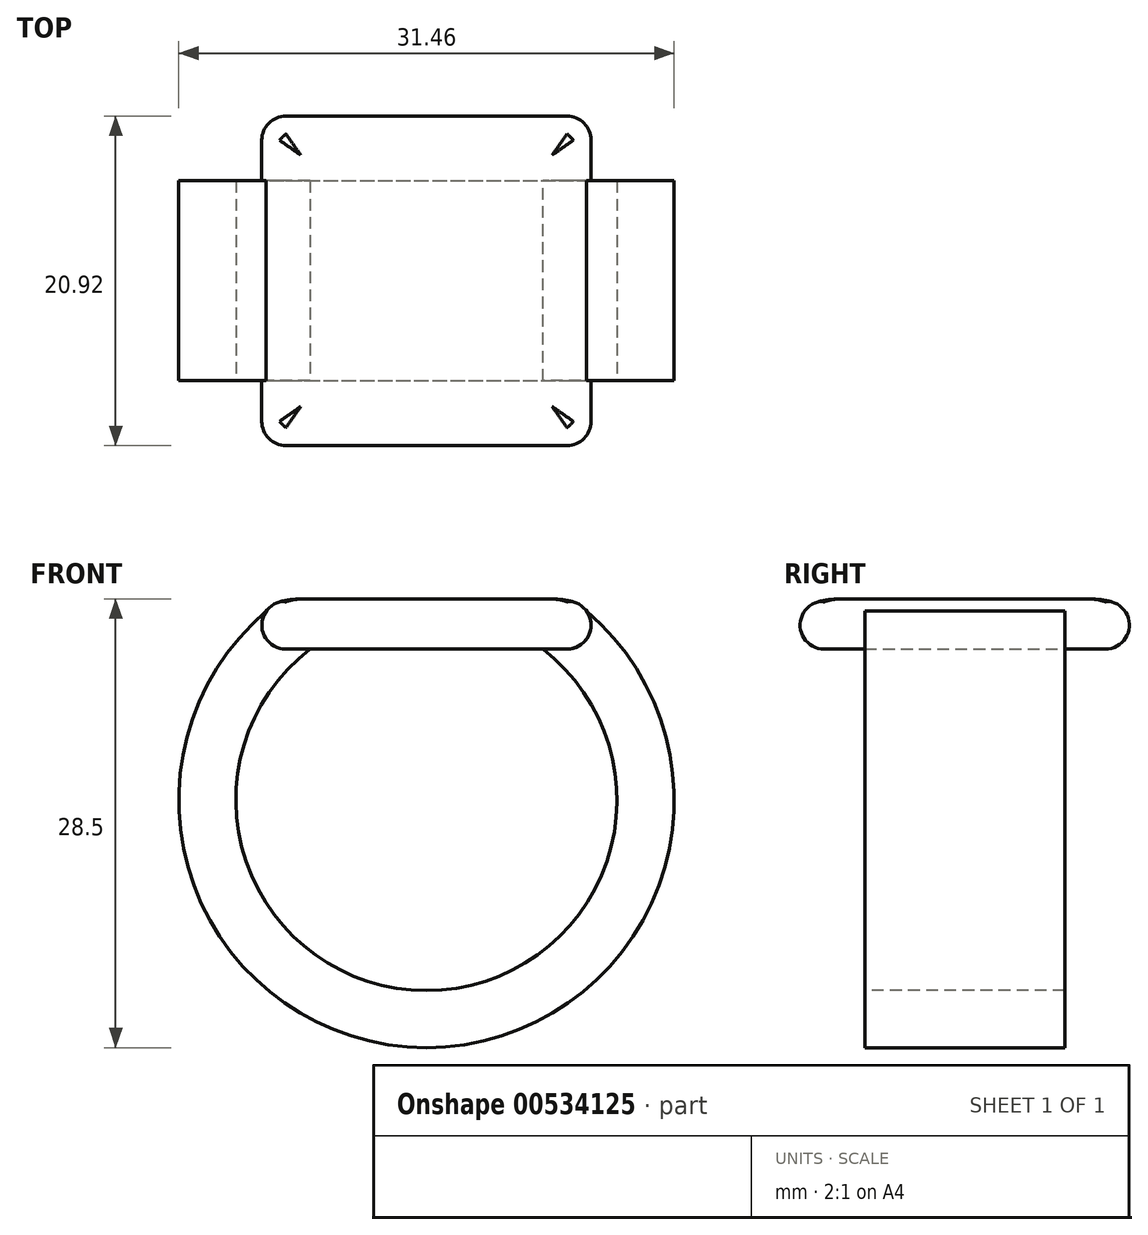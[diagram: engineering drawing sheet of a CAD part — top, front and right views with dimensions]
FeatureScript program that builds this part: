
annotation { "Feature Type Name" : "Feature", "Feature Type Description" : "" }
export const myFeature = defineFeature(function(context is Context, id is Id, definition is map)
    precondition{}
    {
        {
            var Q0;
            Q0=qCreatedBy(makeId("Top.planeOp"),FACE);
            var sketch = newSketch(context, id + "F0", { "sketchPlane" : qUnion([Q0])});
            skLineSegment(sketch, "E0.bottom", {"start": v(12.7, 12.7) * mm, "end": v(-12.7, 12.7) * mm});
            skLineSegment(sketch, "E0.top", {"start": v(12.7, -12.7) * mm, "end": v(-12.7, -12.7) * mm});
            skLineSegment(sketch, "E0.left", {"start": v(12.7, 12.7) * mm, "end": v(12.7, -12.7) * mm});
            skLineSegment(sketch, "E0.right", {"start": v(-12.7, 12.7) * mm, "end": v(-12.7, -12.7) * mm});
            skPoint(sketch, "E0.middle", {"position": v(0, 0) * mm});
            skSolve(sketch);
        }
        {
            var Q0;
            Q0=makeQuery(id+"F0.imprint","IMPRINT",FACE,{"disambiguationData":[TD([[makeQuery(id+"F0.imprint","IMPRINT",EDGE,{"derivedFrom":sQuery(id+"F0.wireOp",EDGE,"E0.bottom")}),1.0]])]});
            extrude(context, id + "F1", {"entities" : qUnion([Q0]), "depth" : 3.17 * mm, "offsetDistance" : 25.4 * mm});
        }
        {
            var Q0;
            Q0=qCreatedBy(makeId("Front.planeOp"),FACE);
            var sketch = newSketch(context, id + "F2", { "sketchPlane" : qUnion([Q0])});
            skArc(sketch, "E1", {"start": v(-10.16, 0) * mm, "mid": v(0, -23.56) * mm, "end": v(10.16, 0) * mm});
            skSolve(sketch);
        }
        {
            var Q0;
            Q0=makeQuery(id+"F1.opExtrude","CAP_FACE",FACE,{"disambiguationData":[OSD([sQuery(id+"F0.wireOp",EDGE,"E0.bottom"),sQuery(id+"F0.wireOp",EDGE,"E0.top"),sQuery(id+"F0.wireOp",EDGE,"E0.left"),sQuery(id+"F0.wireOp",EDGE,"E0.right")])],"isStart":true});
            var sketch = newSketch(context, id + "F3", { "sketchPlane" : qUnion([Q0])});
            skLineSegment(sketch, "E2.bottom", {"start": v(-12.47, -6.35) * mm, "end": v(-7.39, -6.35) * mm});
            skLineSegment(sketch, "E2.top", {"start": v(-12.47, 6.35) * mm, "end": v(-7.39, 6.35) * mm});
            skLineSegment(sketch, "E2.left", {"start": v(-12.47, -6.35) * mm, "end": v(-12.47, 6.35) * mm});
            skLineSegment(sketch, "E2.right", {"start": v(-7.39, -6.35) * mm, "end": v(-7.39, 6.35) * mm});
            skPoint(sketch, "E2.middle", {"position": v(-9.93, 0) * mm});
            skSolve(sketch);
        }
        {
            var Q0;
            Q0 = qSketchRegion(id + "F3", true);
            var Q1;
            Q1 = qConstructionFilter(qBodyType(qCreatedBy(id + "F2" ,EDGE), BodyType.WIRE), ConstructionObject.NO);
            sweep(context, id + "F4", {"operationType" : NewBodyOperationType.ADD, "profiles" : qUnion([Q0]), "path" : qUnion([Q1])});
        }
        {
            var Q0;
            Q0=qCreatedBy(makeId("Front.planeOp"),FACE);
            var sketch = newSketch(context, id + "F5", { "sketchPlane" : qUnion([Q0])});
            skLineSegment(sketch, "E3.0", {"start": v(10.16, 0) * mm, "end": v(7.39, 0) * mm});
            skLineSegment(sketch, "E3.1", {"start": v(10, -2.77) * mm, "end": v(10.16, 0) * mm});
            skArc(sketch, "E3.2", {"start": v(10, -2.77) * mm, "mid": v(8.8, -1.28) * mm, "end": v(7.39, 0) * mm});
            skPoint(sketch, "E4.orphan", {"position": v(-7.39, 0) * mm});
            skPoint(sketch, "E5.orphan", {"position": v(12.7, 0) * mm});
            skPoint(sketch, "E6.trimOffspring.end.orphan", {"position": v(-12.7, 0) * mm});
            skSolve(sketch);
        }
        {
            var Q0;
            Q0 = qSketchRegion(id + "F5", true);
            var Q1;
            Q1=makeQuery(id+"F4.opSweep","SWEPT_FACE",FACE,{"disambiguationData":[OSD([sQuery(id+"F2.wireOp",EDGE,"E1"),sQuery(id+"F3.wireOp",EDGE,"E2.top")])]});
            var Q2;
            Q2=makeQuery(id+"F4.opSweep","SWEPT_FACE",FACE,{"disambiguationData":[OSD([sQuery(id+"F2.wireOp",EDGE,"E1"),sQuery(id+"F3.wireOp",EDGE,"E2.bottom")])]});
            extrude(context, id + "F6", {"entities" : qUnion([Q0]), "operationType" : NewBodyOperationType.ADD, "endBound" : BoundingType.UP_TO_SURFACE, "depth" : 25.4 * mm, "endBoundEntityFace" : qUnion([Q1]), "offsetDistance" : 25.4 * mm, "hasSecondDirection" : true, "secondDirectionBound" : SecondDirectionBoundingType.UP_TO_SURFACE, "secondDirectionOppositeDirection" : true, "secondDirectionDepth" : 25.4 * mm, "secondDirectionBoundEntityFace" : qUnion([Q2])});
        }
        {
            var Q0;
            Q0=makeQuery(id+"F1.opExtrude","CAP_EDGE",EDGE,{"disambiguationData":[OSD([sQuery(id+"F0.wireOp",EDGE,"E0.bottom")])],"isStart":false});
            var Q1;
            Q1=makeQuery(id+"F1.opExtrude","CAP_EDGE",EDGE,{"disambiguationData":[OSD([sQuery(id+"F0.wireOp",EDGE,"E0.right")])],"isStart":false});
            var Q2;
            Q2=makeQuery(id+"F1.opExtrude","CAP_EDGE",EDGE,{"disambiguationData":[OSD([sQuery(id+"F0.wireOp",EDGE,"E0.left")])],"isStart":false});
            var Q3;
            Q3=makeQuery(id+"F1.opExtrude","CAP_EDGE",EDGE,{"disambiguationData":[OSD([sQuery(id+"F0.wireOp",EDGE,"E0.top")])],"isStart":false});
            fillet(context, id + "F7", {"entities" : qUnion([Q0, Q1, Q2, Q3]), "radius" : 5.08 * mm, "tangentPropagation" : true, "allowEdgeOverflow" : false});
        }
        {
            var Q0;
            Q0=makeQuery(id+"F7.opFillet","BLEND_FACE",FACE,{"disambiguationData":[OSD([sQuery(id+"F0.wireOp",EDGE,"E0.top")])]});
            var Q1;
            Q1=makeQuery(id+"F7.opFillet","BLEND_FACE",FACE,{"disambiguationData":[OSD([sQuery(id+"F0.wireOp",EDGE,"E0.left")])]});
            var Q2;
            Q2=makeQuery(id+"F7.opFillet","BLEND_FACE",FACE,{"disambiguationData":[OSD([sQuery(id+"F0.wireOp",EDGE,"E0.bottom")])]});
            var Q3;
            Q3=makeQuery(id+"F7.opFillet","BLEND_FACE",FACE,{"disambiguationData":[OSD([sQuery(id+"F0.wireOp",EDGE,"E0.right")])]});
            fillet(context, id + "F8", {"entities" : qUnion([Q0, Q1, Q2, Q3]), "radius" : 1.52 * mm, "tangentPropagation" : true, "allowEdgeOverflow" : false});
        }
    });
